# Revit family: Tempra BIM 130831
name_source: partatom
category: Air Terminals
revit_build: Autodesk Revit MEP 2013 (Build: 20120221_2030(x64)
units: mm (PartAtom-declared; Revit-internal decimal feet)

## types (6) — shared parameters
AC Frequency Input = 50Hz nominal
AC Voltage Input = 240
Accessories = 100mm High Rise Kit - 449011
Country of Manufacture = UK
Default Elevation = 1200 mm
Heat Exchanger Overall length = 496 mm  [stored 1.6273 ft]
Heat Exchanger Wall Sleeve = 321 mm  [stored 1.05315 ft]
Height = 260 mm  [stored 0.853018 ft]
IP Rating = IPX4
Manufacturer - Name = Vent-Axia Ltd
Manufacturer - Website = www.vent-axia.com
Operating Temperature = (-5C to +40C)
Operational and Maintenance Manual = http://www.vent-axia.com
Sub Type = Single Room Heat Recovery
Unit Depth = 117 mm  [stored 0.383858 ft]
Warranty period = Unit 2 years                                    Motor 5 years
Weight = 3kgs
Width = 190 mm

## per-type parameters (varying)
| type | Category | Controllers Supply | Family | Fan Unit Supply | Motor Rating | Part Number | Product Description |
| Tempra P | Lo Carbon Tempra |  | TEMPRA P |  | 2.4 W (max) | 443312 | Lo Carbon Tempra P Single Room Heat Recovery Unit with pullcord |
| Tempra T | Lo Carbon Tempra |  | Tempra T |  | 26.6 Watts (Boost) | 443310 | Lo Carbon Tempra T Single Room Heat Recovery Unit with overrun timer |
| Tempra HTP | Lo Carbon Tempra |  | Tempra HTP |  | 26.6 Watts (Boost) | 443311 | Lo Carbon Tempra HTP Single Room Heat Recovery Unit with Humidistat, pullcord and overrun timer |
| Tempra SELV P | Lo Carbon Tempra | 220-240 V AC with 24V DC SELV OUTPUT | Tempra SELV P | 24V DC SELV | 26.6 Watts (Boost) | 444368 | Lo Carbon Tempra P SELV Single Room Heat Recovery Unit with pullcord |
| Tempra SELV T | Lo Carbon Tempra | 220-240 V AC with 24V DC SELV OUTPUT | TEMPRA SELV T | 24V DC SELV | 26.6 Watts (Boost) | 444370 | Lo Carbon Tempra SELV HTP Single Room Heat Recovery Unit with Humidistat, pullcord and overrun timer |
| Tempra SELV HTP | Lo Carbon Tempra SELV | 220-240 V AC with 24V DC SELV OUTPUT | TEMPRA SELV HTP | 24V DC SELV | 26.6 Watts (Boost) | 444370 | Lo Carbon Tempra SELV HTP Single Room Heat Recovery Unit with Humidistat, pullcord and overrun timer |

note: source unit labels omitted for AC Voltage Input — the stored unit's dimension contradicts the parameter name (converter mislabeling)

note: [stored X ft] marks values corroborated as IEEE doubles in the binary element streams (Revit-internal decimal feet)

## geometry (parser evidence)
native form markers: Sweep x1
no freeform markers — native parametric forms only
